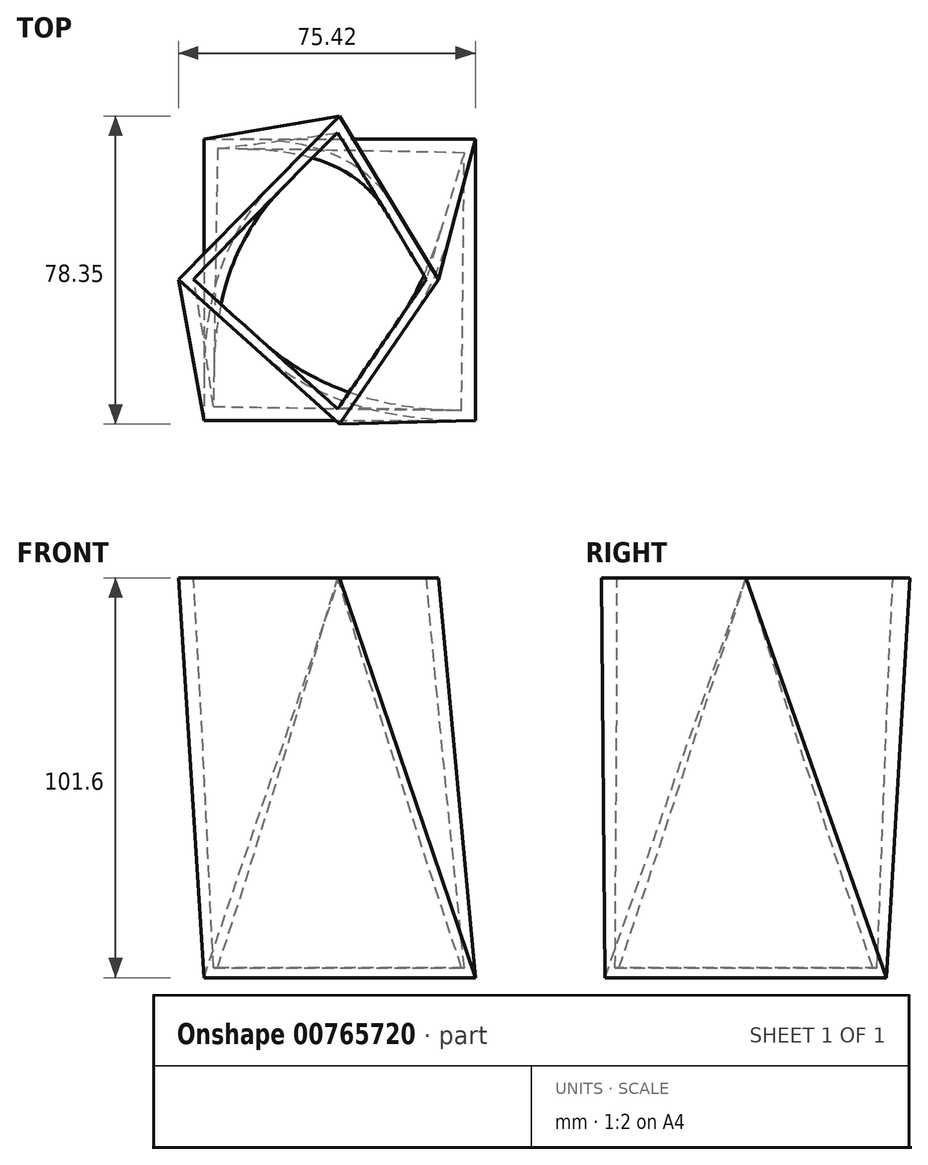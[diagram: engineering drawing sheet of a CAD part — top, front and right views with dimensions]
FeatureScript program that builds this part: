
annotation { "Feature Type Name" : "Feature", "Feature Type Description" : "" }
export const myFeature = defineFeature(function(context is Context, id is Id, definition is map)
    precondition{}
    {
        {
            var Q0;
            Q0=qCreatedBy(makeId("Top.planeOp"),FACE);
            var sketch = newSketch(context, id + "F0", { "sketchPlane" : qUnion([Q0])});
            skLineSegment(sketch, "E0.bottom", {"start": v(-34.49, 35.76) * mm, "end": v(34.49, 35.76) * mm});
            skLineSegment(sketch, "E0.top", {"start": v(-34.49, -35.76) * mm, "end": v(34.49, -35.76) * mm});
            skLineSegment(sketch, "E0.left", {"start": v(-34.49, 35.76) * mm, "end": v(-34.49, -35.76) * mm});
            skLineSegment(sketch, "E0.right", {"start": v(34.49, 35.76) * mm, "end": v(34.49, -35.76) * mm});
            skPoint(sketch, "E0.middle", {"position": v(0, 0) * mm});
            skSolve(sketch);
        }
        {
            var Q0;
            Q0=qCreatedBy(makeId("Top.planeOp"),FACE);
            cPlane(context, id + "F1", {"entities" : qUnion([Q0]), "cplaneType" : CPlaneType.OFFSET, "offset" : 101.6 * mm, "width" : 152.4 * mm, "height" : 152.4 * mm});
        }
        {
            var Q0;
            Q0=qCreatedBy(id+"F1.planeOp",FACE);
            var sketch = newSketch(context, id + "F2", { "sketchPlane" : qUnion([Q0])});
            skLineSegment(sketch, "E1", {"start": v(0, 41.62) * mm, "end": v(-40.93, 0) * mm});
            skLineSegment(sketch, "E2", {"start": v(-40.93, 0) * mm, "end": v(0, -36.73) * mm});
            skLineSegment(sketch, "E3", {"start": v(0, -36.73) * mm, "end": v(25.1, 0) * mm});
            skLineSegment(sketch, "E4", {"start": v(25.1, 0) * mm, "end": v(0, 41.62) * mm});
            skSolve(sketch);
        }
        {
            var Q0;
            Q0=makeQuery(id+"F0.imprint","IMPRINT",FACE,{"disambiguationData":[TD([[makeQuery(id+"F0.imprint","IMPRINT",EDGE,{"derivedFrom":sQuery(id+"F0.wireOp",EDGE,"E0.bottom")}),-1.0]])]});
            var Q1;
            Q1=makeQuery(id+"F2.imprint","IMPRINT",FACE,{"disambiguationData":[TD([[makeQuery(id+"F2.imprint","IMPRINT",EDGE,{"derivedFrom":sQuery(id+"F2.wireOp",EDGE,"E1")}),1.0]])]});
            loft(context, id + "F3", {"sheetProfilesArray" : [{ "sheetProfileEntities" : qUnion([Q0]) }, { "sheetProfileEntities" : qUnion([Q1]) }]});
        }
        {
            var Q0;
            Q0=makeQuery(id+"F3.opLoft","CAP_FACE",FACE,{"disambiguationData":[OSD([makeQuery(id+"F2.imprint","IMPRINT",FACE,{"disambiguationData":[TD([[makeQuery(id+"F2.imprint","IMPRINT",EDGE,{"derivedFrom":sQuery(id+"F2.wireOp",EDGE,"E1")}),1.0]])]})])],"isStart":true});
            shell(context, id + "F4", {"entities" : qUnion([Q0]), "thickness" : 2.54 * mm});
        }
    });
